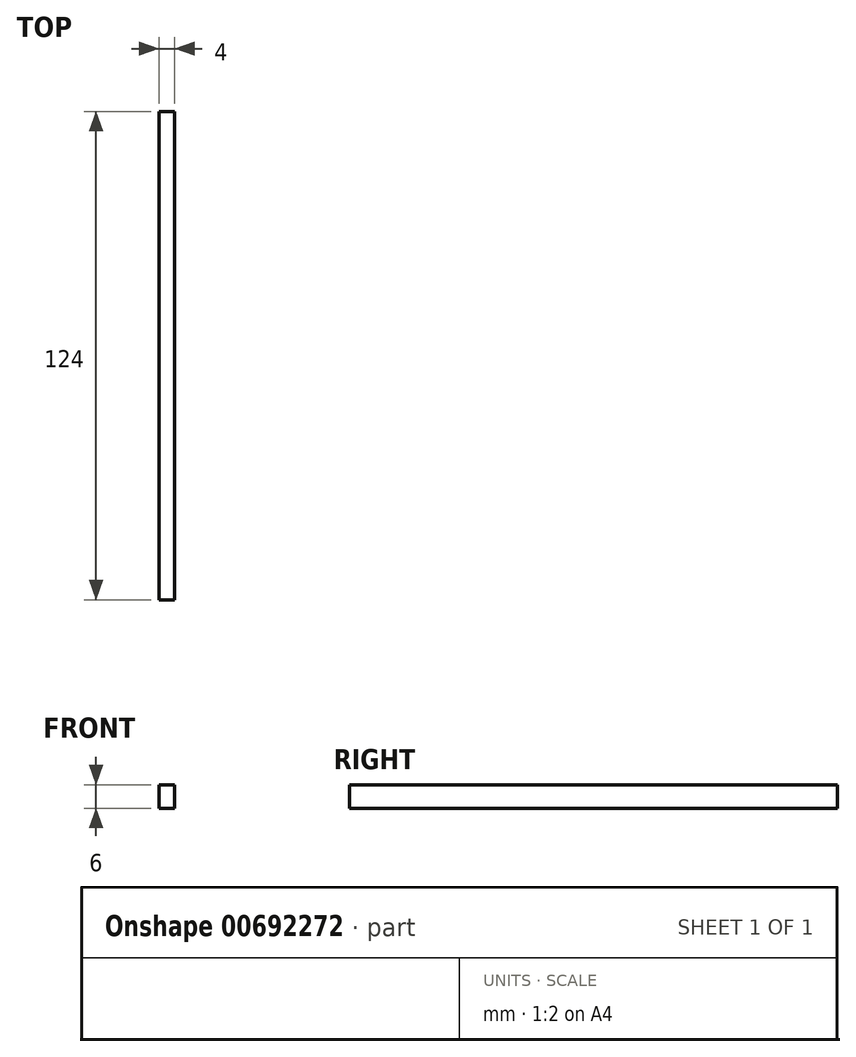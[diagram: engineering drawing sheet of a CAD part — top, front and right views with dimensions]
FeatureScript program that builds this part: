
annotation { "Feature Type Name" : "Feature", "Feature Type Description" : "" }
export const myFeature = defineFeature(function(context is Context, id is Id, definition is map)
    precondition{}
    {
        {
            var Q0;
            Q0=qCreatedBy(makeId("Top.planeOp"),FACE);
            var sketch = newSketch(context, id + "F0", { "sketchPlane" : qUnion([Q0])});
            skLineSegment(sketch, "E0.bottom", {"start": v(0, 0) * mm, "end": v(4, 0) * mm});
            skLineSegment(sketch, "E0.top", {"start": v(0, 124) * mm, "end": v(4, 124) * mm});
            skLineSegment(sketch, "E0.left", {"start": v(0, 0) * mm, "end": v(0, 124) * mm});
            skLineSegment(sketch, "E0.right", {"start": v(4, 0) * mm, "end": v(4, 124) * mm});
            skSolve(sketch);
        }
        {
            var Q0;
            Q0 = qSketchRegion(id + "F0", true);
            extrude(context, id + "F1", {"entities" : qUnion([Q0]), "depth" : 6 * mm, "offsetDistance" : 25.4 * mm});
        }
    });
